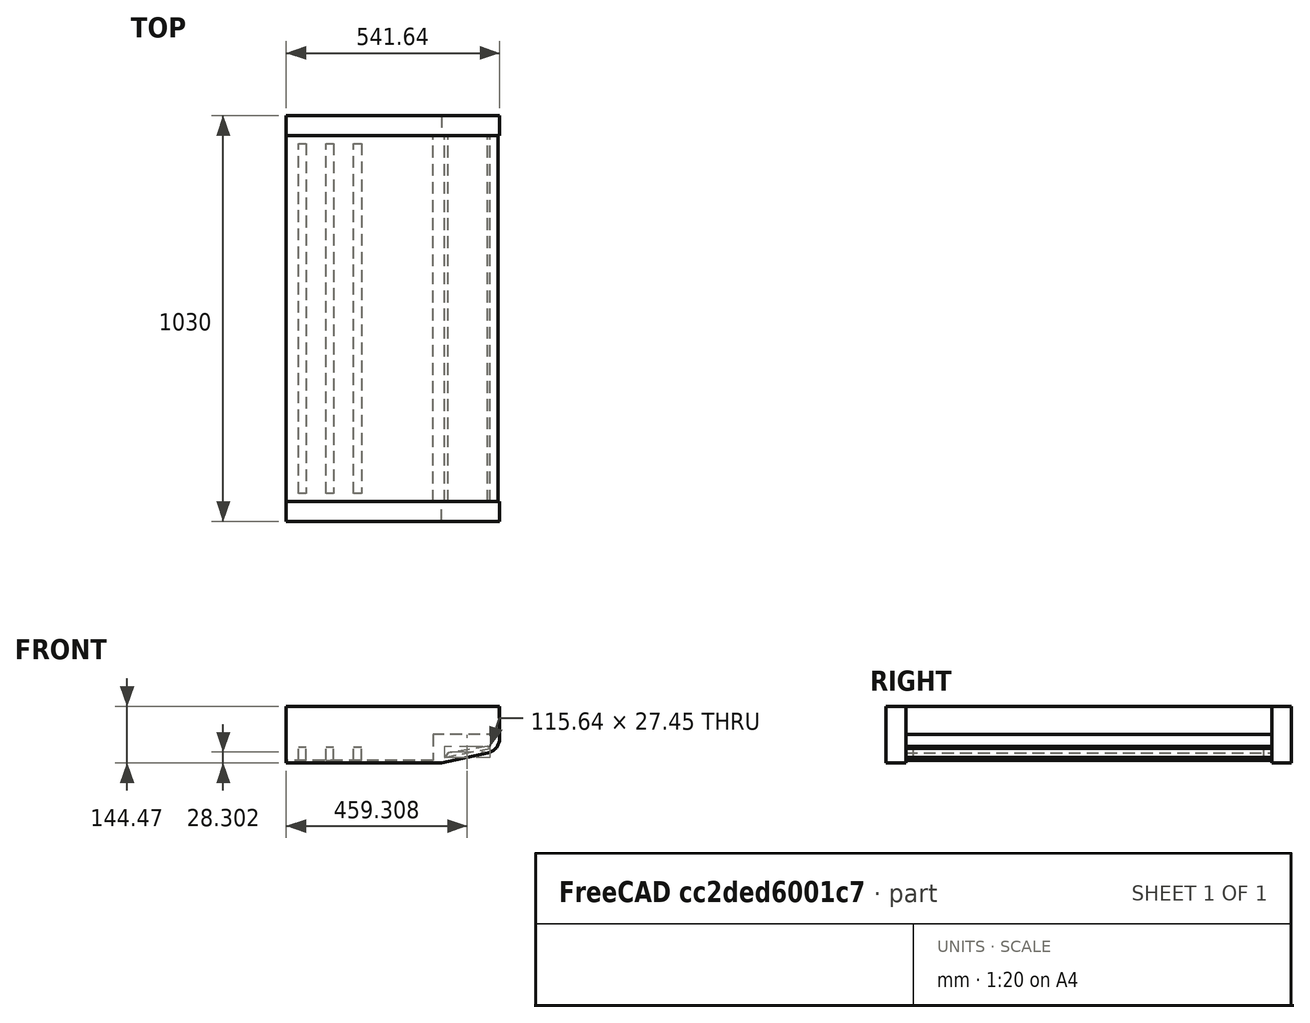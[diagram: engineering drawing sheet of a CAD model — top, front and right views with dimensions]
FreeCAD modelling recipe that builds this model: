
FCSTD DOCUMENT  (FreeCAD 0.17R10000 (Git))
Label: Air conditionning
License: All rights reserved
LicenseURL: http://en.wikipedia.org/wiki/All_rights_reserved
objects: Sketcher::SketchObject×5, PartDesign::Pad×4, Mesh::Feature×1, PartDesign::Plane×1, PartDesign::Pocket×1, PartDesign::Body×1
note: 17 computed .brp shape members not serialized (recipe doc carries the construction recipe); baked Part::Feature solids carry a one-line shape summary decoded from their .brp

FEATURE [Mesh::Feature] Mesh064
FEATURE [Sketcher::SketchObject] Sketch
  MapMode = 5
  Placement = pos=(0,0,0) rot=(1,0,0;1.5708rad)
  Support = -> [XZ_Plane]
  sketch-geometry (6):
    g0: LineSegment StartX=0 StartY=0 StartZ=0 EndX=394.049 EndY=0 EndZ=0
    g1: LineSegment StartX=394.049 StartY=0 StartZ=0 EndX=512.796 EndY=26.1931 EndZ=0
    g2: ArcOfCircle CenterX=504.878 CenterY=62.0912 CenterZ=0 NormalX=0 NormalY=0 NormalZ=1 Radius=36.7611 StartAngle=4.92949 EndAngle=6.28319
    g3: LineSegment StartX=541.639 StartY=62.0912 StartZ=0 EndX=541.639 EndY=144.471 EndZ=0
    g4: LineSegment StartX=541.639 StartY=144.471 StartZ=0 EndX=0 EndY=144.471 EndZ=0
    g5: LineSegment StartX=0 StartY=144.471 StartZ=0 EndX=0 EndY=0 EndZ=0
  constraints (11):
    c: Coincident(g-1,g0)
    c: Horizontal(g0)
    c: Coincident(g0,g1)
    c: Tangent(g1,g2) = -1.5708
    c: Tangent(g2,g3) = -1.5708
    c: Coincident(g3,g4)
    c: PointOnObject(g4,g-2)
    c: Horizontal(g4)
    c: Coincident(g4,g5)
    c: Coincident(g5,g0)
    c: Vertical(g3)
FEATURE [PartDesign::Plane] DatumPlane
  MapMode = 5
  Placement = pos=(0,1030,0) rot=(1,0,0;1.5708rad)
  Support = -> [XZ_Plane]
  superPlacement = pos=(0,0,-1030) rot=(0,0,1;0rad)
FEATURE [Sketcher::SketchObject] Sketch001
  MapMode = 5
  Placement = pos=(0,1030,0) rot=(1,0,0;1.5708rad)
  Support = -> [DatumPlane]
  sketch-geometry (6):
    g0: LineSegment StartX=0 StartY=0 StartZ=0 EndX=394.049 EndY=0 EndZ=0
    g1: LineSegment StartX=394.049 StartY=0 StartZ=0 EndX=512.796 EndY=26.1931 EndZ=0
    g2: ArcOfCircle CenterX=504.878 CenterY=62.0912 CenterZ=0 NormalX=0 NormalY=0 NormalZ=1 Radius=36.7611 StartAngle=4.92949 EndAngle=6.28319
    g3: LineSegment StartX=541.639 StartY=62.0912 StartZ=0 EndX=541.639 EndY=144.471 EndZ=0
    g4: LineSegment StartX=541.639 StartY=144.471 StartZ=0 EndX=0 EndY=144.471 EndZ=0
    g5: LineSegment StartX=0 StartY=144.471 StartZ=0 EndX=0 EndY=0 EndZ=0
  constraints (11):
    c: Coincident(g-1,g0)
    c: Horizontal(g0)
    c: Coincident(g0,g1)
    c: Tangent(g1,g2) = -1.5708
    c: Tangent(g2,g3) = -1.5708
    c: Coincident(g3,g4)
    c: PointOnObject(g4,g-2)
    c: Horizontal(g4)
    c: Coincident(g4,g5)
    c: Coincident(g5,g0)
    c: Vertical(g3)
FEATURE [PartDesign::Pad] Pad
  Length = 50
  Length2 = 100
  Placement = pos=(0,0,0) rot=(1,0,0;1.5708rad)
  Profile = -> Sketch
  Reversed = true
  Type = 0
FEATURE [Sketcher::SketchObject] Sketch002
  MapMode = 5
  Placement = pos=(0,50,0) rot=(-1,0,0;1.5708rad)
  Support = -> [Pad]
  sketch-geometry (6):
    g0: LineSegment StartX=0 StartY=-144.145 StartZ=0 EndX=538.483 EndY=-144.145 EndZ=0
    g1: LineSegment StartX=538.483 StartY=-144.145 StartZ=0 EndX=538.483 EndY=-72.28 EndZ=0
    g2: LineSegment StartX=538.483 StartY=-72.28 StartZ=0 EndX=372.794 EndY=-72.28 EndZ=0
    g3: LineSegment StartX=372.794 StartY=-72.28 StartZ=0 EndX=372.794 EndY=-6.40368 EndZ=0
    g4: LineSegment StartX=372.794 StartY=-6.40368 StartZ=0 EndX=0 EndY=-6.40368 EndZ=0
    g5: LineSegment StartX=0 StartY=-6.40368 StartZ=0 EndX=0 EndY=-144.145 EndZ=0
  constraints (13):
    c: PointOnObject(g0,g-2)
    c: Horizontal(g0)
    c: Coincident(g0,g1)
    c: Vertical(g1)
    c: Coincident(g1,g2)
    c: Horizontal(g2)
    c: Coincident(g2,g3)
    c: Vertical(g3)
    c: Coincident(g3,g4)
    c: PointOnObject(g4,g-2)
    c: Horizontal(g4)
    c: Coincident(g4,g5)
    c: Coincident(g5,g0)
FEATURE [PartDesign::Pad] Pad001
  BaseFeature = -> Pad
  Length = 930
  Length2 = 100
  Placement = pos=(0,0,0) rot=(1,0,0;1.5708rad)
  Profile = -> Sketch002
  Type = 0
FEATURE [PartDesign::Pad] Pad002
  BaseFeature = -> Pad001
  Length = 50
  Length2 = 100
  Placement = pos=(0,0,0) rot=(1,0,0;1.5708rad)
  Profile = -> Sketch001
  Type = 0
FEATURE [Sketcher::SketchObject] Sketch003
  MapMode = 5
  Placement = pos=(0,50,0) rot=(-1,0,0;1.5708rad)
  Support = -> [Pad002]
  sketch-geometry (4):
    g0: LineSegment StartX=401.487 StartY=-14.5775 StartZ=0 EndX=517.129 EndY=-37.0353 EndZ=0
    g1: LineSegment StartX=517.129 StartY=-37.0353 StartZ=0 EndX=511.281 EndY=-42.026 EndZ=0
    g2: LineSegment StartX=511.281 StartY=-42.026 StartZ=0 EndX=410.97 EndY=-25.5569 EndZ=0
    g3: LineSegment StartX=410.97 StartY=-25.5569 StartZ=0 EndX=401.487 EndY=-14.5775 EndZ=0
  constraints (4):
    c: Coincident(g0,g1)
    c: Coincident(g1,g2)
    c: Coincident(g2,g3)
    c: Coincident(g3,g0)
FEATURE [PartDesign::Pad] Pad003
  BaseFeature = -> Pad002
  Length = 930
  Length2 = 100
  Placement = pos=(0,0,0) rot=(1,0,0;1.5708rad)
  Profile = -> Sketch003
  Type = 0
FEATURE [Sketcher::SketchObject] Sketch004
  ExternalGeometry = -> [Pad003]
  MapMode = 5
  Placement = pos=(0,0,6.40368) rot=(1,0,0;3.14159rad)
  Support = -> [Pad003]
  sketch-geometry (12):
    g0: LineSegment StartX=190.629 StartY=-70 StartZ=0 EndX=170.629 EndY=-70 EndZ=0
    g1: LineSegment StartX=170.629 StartY=-70 StartZ=0 EndX=170.629 EndY=-960 EndZ=0
    g2: LineSegment StartX=170.629 StartY=-960 StartZ=0 EndX=190.629 EndY=-960 EndZ=0
    g3: LineSegment StartX=190.629 StartY=-960 StartZ=0 EndX=190.629 EndY=-70 EndZ=0
    g4: LineSegment StartX=120.629 StartY=-70 StartZ=0 EndX=100.629 EndY=-70 EndZ=0
    g5: LineSegment StartX=100.629 StartY=-70 StartZ=0 EndX=100.629 EndY=-960 EndZ=0
    g6: LineSegment StartX=100.629 StartY=-960 StartZ=0 EndX=120.629 EndY=-960 EndZ=0
    g7: LineSegment StartX=120.629 StartY=-960 StartZ=0 EndX=120.629 EndY=-70 EndZ=0
    g8: LineSegment StartX=50.6292 StartY=-70 StartZ=0 EndX=30.6292 EndY=-70 EndZ=0
    g9: LineSegment StartX=30.6292 StartY=-70 StartZ=0 EndX=30.6292 EndY=-960 EndZ=0
    g10: LineSegment StartX=30.6292 StartY=-960 StartZ=0 EndX=50.6292 EndY=-960 EndZ=0
    g11: LineSegment StartX=50.6292 StartY=-960 StartZ=0 EndX=50.6292 EndY=-70 EndZ=0
  constraints (35):
    c: Coincident(g0,g1)
    c: Coincident(g1,g2)
    c: Coincident(g2,g3)
    c: Coincident(g3,g0)
    c: Horizontal(g0)
    c: Horizontal(g2)
    c: Vertical(g1)
    c: Vertical(g3)
    c: Coincident(g4,g5)
    c: Coincident(g5,g6)
    c: Coincident(g6,g7)
    c: Coincident(g7,g4)
    c: Horizontal(g4)
    c: Horizontal(g6)
    c: Vertical(g5)
    c: Vertical(g7)
    c: Coincident(g8,g9)
    c: Coincident(g9,g10)
    c: Coincident(g10,g11)
    c: Coincident(g11,g8)
    c: Horizontal(g8)
    c: Horizontal(g10)
    c: Vertical(g9)
    c: Vertical(g11)
    c: DistanceX(g8,g8) = 20
    c: DistanceX(g4,g4) = 20
    c: DistanceX(g0,g0) = 20
    c: DistanceX(g8,g4) = 50
    c: DistanceX(g4,g0) = 50
    c: DistanceY(g8,g-3) = 20
    c: DistanceY(g4,g-3) = 20
    c: DistanceY(g0,g-3) = 20
    c: DistanceY(g-3,g2) = 20
    c: DistanceY(g-3,g6) = 20
    c: DistanceY(g-3,g10) = 20
FEATURE [PartDesign::Pocket] Pocket
  BaseFeature = -> Pad003
  Length = 35
  Placement = pos=(0,0,0) rot=(1,0,0;1.5708rad)
  Profile = -> Sketch004
  Type = 0
FEATURE [PartDesign::Body] Body
  Group = -> [Sketch,DatumPlane,Sketch001,Pad,Sketch002,Pad001,Pad002,Sketch003,Pad003,Sketch004,Pocket]
  Origin = -> BodyOrigin
  Tip = -> Pocket
